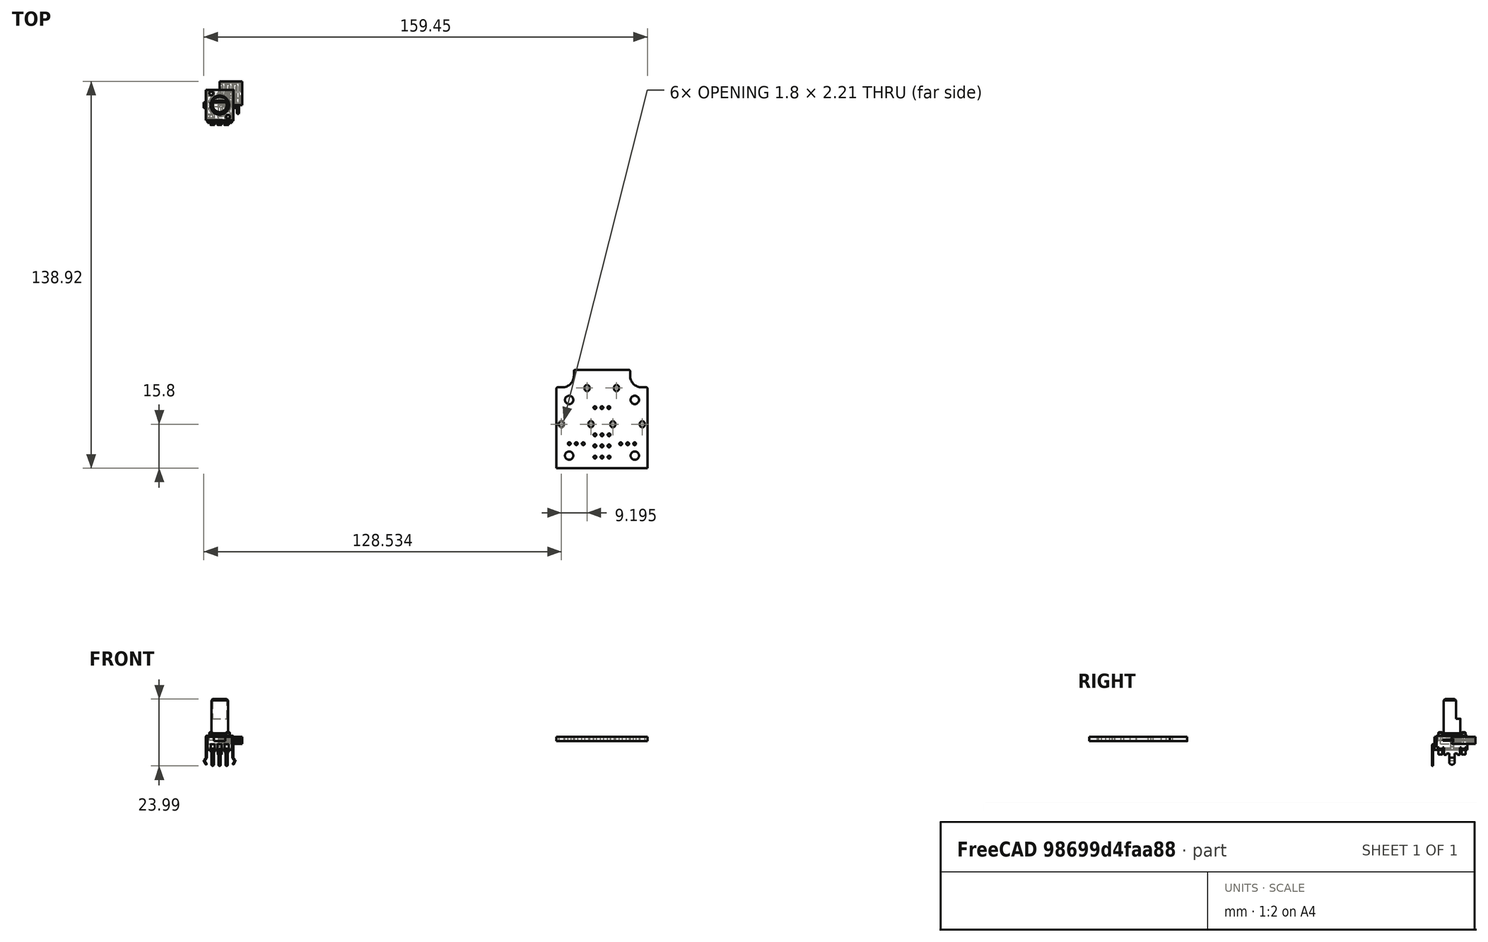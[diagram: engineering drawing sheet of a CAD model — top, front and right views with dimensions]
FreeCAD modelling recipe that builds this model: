
FCSTD DOCUMENT  (FreeCAD 0.20R25645 (Git))
Label: PotBoard
License: All rights reserved
LicenseURL: http://en.wikipedia.org/wiki/All_rights_reserved
objects: Part::Feature×7, App::Part×7, App::Link×4, PartDesign::CoordinateSystem×1, Sketcher::SketchObject×1
note: 9 computed .brp shape members not serialized (recipe doc carries the construction recipe); baked Part::Feature solids carry a one-line shape summary decoded from their .brp

FEATURE [PartDesign::CoordinateSystem] Local_CS_873f
  AttacherType = Attacher::AttachEngine3D
FEATURE [Part::Feature] Pcb_873f
  shape: bbox 32.7 x 35.3 x 1.6 mm, 86 faces (baked)
FEATURE [Sketcher::SketchObject] PCB_Sketch_873f
  FullyConstrained = false
  sketch-geometry (126):
    g0: LineSegment StartX=121.055 StartY=-101.87 StartZ=0 EndX=121.055 EndY=-130.418 EndZ=0
    g1: LineSegment StartX=127.305 StartY=-95.6198 StartZ=0 EndX=127.305 EndY=-97.218 EndZ=0
    g2: LineSegment StartX=123.153 StartY=-101.37 StartZ=0 EndX=121.555 EndY=-101.37 EndZ=0
    g3: LineSegment StartX=153.251 StartY=-101.37 StartZ=0 EndX=151.653 EndY=-101.37 EndZ=0
    g4: LineSegment StartX=153.751 StartY=-130.418 StartZ=0 EndX=153.751 EndY=-101.87 EndZ=0
    g5: LineSegment StartX=147.001 StartY=-95.1202 StartZ=0 EndX=127.805 EndY=-95.1202 EndZ=0
    g6: LineSegment StartX=121.055 StartY=-130.418 StartZ=0 EndX=153.751 EndY=-130.418 EndZ=0
    g7: LineSegment StartX=147.501 StartY=-97.218 StartZ=0 EndX=147.501 EndY=-95.6198 EndZ=0
    g8: BSplineCurve PolesCount=4 KnotsCount=2 Degree=3 IsPeriodic=0
    g9: BSplineCurve PolesCount=4 KnotsCount=2 Degree=3 IsPeriodic=0
    g10: BSplineCurve PolesCount=4 KnotsCount=2 Degree=3 IsPeriodic=0
    g11: BSplineCurve PolesCount=4 KnotsCount=2 Degree=3 IsPeriodic=0
    g12: BSplineCurve PolesCount=4 KnotsCount=2 Degree=3 IsPeriodic=0
    g13: BSplineCurve PolesCount=4 KnotsCount=2 Degree=3 IsPeriodic=0
    g14: BSplineCurve PolesCount=4 KnotsCount=2 Degree=3 IsPeriodic=0
    g15: BSplineCurve PolesCount=4 KnotsCount=2 Degree=3 IsPeriodic=0
    g16: BSplineCurve PolesCount=4 KnotsCount=2 Degree=3 IsPeriodic=0
    g17: BSplineCurve PolesCount=4 KnotsCount=2 Degree=3 IsPeriodic=0
    g18: BSplineCurve PolesCount=4 KnotsCount=2 Degree=3 IsPeriodic=0
    g19: BSplineCurve PolesCount=4 KnotsCount=2 Degree=3 IsPeriodic=0
    g20: BSplineCurve PolesCount=4 KnotsCount=2 Degree=3 IsPeriodic=0
    g21: BSplineCurve PolesCount=4 KnotsCount=2 Degree=3 IsPeriodic=0
    g22: BSplineCurve PolesCount=4 KnotsCount=2 Degree=3 IsPeriodic=0
    g23: BSplineCurve PolesCount=4 KnotsCount=2 Degree=3 IsPeriodic=0
    g24: ArcOfCircle CenterX=123.153 CenterY=-97.218 CenterZ=0 NormalX=0 NormalY=0 NormalZ=1 AngleXU=0 Radius=4.1522 StartAngle=4.71239 EndAngle=6.28319
    g25: ArcOfCircle CenterX=151.653 CenterY=-97.218 CenterZ=0 NormalX=0 NormalY=0 NormalZ=1 AngleXU=0 Radius=4.1522 StartAngle=3.14159 EndAngle=4.71239
    g26: Circle CenterX=125.603 CenterY=-125.918 CenterZ=0 NormalX=0 NormalY=0 NormalZ=1 AngleXU=0 Radius=1.5
    g27: Circle CenterX=149.203 CenterY=-125.918 CenterZ=0 NormalX=0 NormalY=0 NormalZ=1 AngleXU=0 Radius=1.5
    g28: Circle CenterX=149.203 CenterY=-105.918 CenterZ=0 NormalX=0 NormalY=0 NormalZ=1 AngleXU=0 Radius=1.5
    g29: Circle CenterX=125.603 CenterY=-105.918 CenterZ=0 NormalX=0 NormalY=0 NormalZ=1 AngleXU=0 Radius=1.5
    g30-g33: Circle x4 (B-spline internal-alignment scaffolding for g8; pole/knot coordinates omitted)
    g34: GeomPoint X=153.751 Y=-101.87 Z=0
    g35: GeomPoint X=153.713 Y=-101.679 Z=0
    g36-g39: Circle x4 (B-spline internal-alignment scaffolding for g9; pole/knot coordinates omitted)
    g40: GeomPoint X=121.555 Y=-101.37 Z=0
    g41: GeomPoint X=121.364 Y=-101.408 Z=0
    g42-g45: Circle x4 (B-spline internal-alignment scaffolding for g10; pole/knot coordinates omitted)
    g46: GeomPoint X=153.442 Y=-101.408 Z=0
    g47: GeomPoint X=153.251 Y=-101.37 Z=0
    g48-g51: Circle x4 (B-spline internal-alignment scaffolding for g11; pole/knot coordinates omitted)
    g52: GeomPoint X=127.805 Y=-95.1202 Z=0
    g53: GeomPoint X=127.614 Y=-95.1582 Z=0
    g54-g57: Circle x4 (B-spline internal-alignment scaffolding for g12; pole/knot coordinates omitted)
    g58: GeomPoint X=147.354 Y=-95.2666 Z=0
    g59: GeomPoint X=147.192 Y=-95.1582 Z=0
    g60-g63: Circle x4 (B-spline internal-alignment scaffolding for g13; pole/knot coordinates omitted)
    g64: GeomPoint X=147.192 Y=-95.1582 Z=0
    g65: GeomPoint X=147.001 Y=-95.1202 Z=0
    g66-g69: Circle x4 (B-spline internal-alignment scaffolding for g14; pole/knot coordinates omitted)
    g70: GeomPoint X=147.463 Y=-95.4287 Z=0
    g71: GeomPoint X=147.354 Y=-95.2666 Z=0
    g72-g75: Circle x4 (B-spline internal-alignment scaffolding for g15; pole/knot coordinates omitted)
    g76: GeomPoint X=147.501 Y=-95.6198 Z=0
    g77: GeomPoint X=147.463 Y=-95.4287 Z=0
    g78-g81: Circle x4 (B-spline internal-alignment scaffolding for g16; pole/knot coordinates omitted)
    g82: GeomPoint X=121.364 Y=-101.408 Z=0
    g83: GeomPoint X=121.202 Y=-101.517 Z=0
    g84-g87: Circle x4 (B-spline internal-alignment scaffolding for g17; pole/knot coordinates omitted)
    g88: GeomPoint X=153.604 Y=-101.517 Z=0
    g89: GeomPoint X=153.442 Y=-101.408 Z=0
    g90-g93: Circle x4 (B-spline internal-alignment scaffolding for g18; pole/knot coordinates omitted)
    g94: GeomPoint X=153.713 Y=-101.679 Z=0
    g95: GeomPoint X=153.604 Y=-101.517 Z=0
    g96-g99: Circle x4 (B-spline internal-alignment scaffolding for g19; pole/knot coordinates omitted)
    g100: GeomPoint X=127.343 Y=-95.4287 Z=0
    g101: GeomPoint X=127.305 Y=-95.6198 Z=0
    g102-g105: Circle x4 (B-spline internal-alignment scaffolding for g20; pole/knot coordinates omitted)
    g106: GeomPoint X=127.614 Y=-95.1582 Z=0
    g107: GeomPoint X=127.452 Y=-95.2666 Z=0
    g108-g111: Circle x4 (B-spline internal-alignment scaffolding for g21; pole/knot coordinates omitted)
    g112: GeomPoint X=127.452 Y=-95.2666 Z=0
    g113: GeomPoint X=127.343 Y=-95.4287 Z=0
    g114-g117: Circle x4 (B-spline internal-alignment scaffolding for g22; pole/knot coordinates omitted)
    g118: GeomPoint X=121.093 Y=-101.679 Z=0
    g119: GeomPoint X=121.055 Y=-101.87 Z=0
    g120-g123: Circle x4 (B-spline internal-alignment scaffolding for g23; pole/knot coordinates omitted)
    g124: GeomPoint X=121.202 Y=-101.517 Z=0
    g125: GeomPoint X=121.093 Y=-101.679 Z=0
  constraints (42):
    c: Coincident(g0,g6)
    c: Coincident(g0,g22)
    c: Coincident(g22,g23)
    c: Coincident(g23,g16)
    c: Coincident(g16,g9)
    c: Coincident(g2,g9)
    c: Coincident(g24,g2)
    c: Coincident(g1,g24)
    c: Coincident(g19,g1)
    c: Coincident(g21,g19)
    c: Coincident(g21,g20)
    c: Coincident(g20,g11)
    c: Coincident(g5,g11)
    c: Coincident(g5,g13)
    c: Coincident(g13,g12)
    c: Coincident(g14,g12)
    c: Coincident(g15,g14)
    c: Coincident(g25,g7)
    c: Coincident(g15,g7)
    c: Coincident(g25,g3)
    c: Coincident(g10,g3)
    c: Coincident(g10,g17)
    c: Coincident(g18,g17)
    c: Coincident(g8,g18)
    c: Coincident(g6,g4)
    c: Coincident(g8,g4)
    c: InternalAlignment(g30-g35 -> g8) x6
    c: InternalAlignment(g36-g41 -> g9) x6
    c: InternalAlignment(g42-g47 -> g10) x6
    c: InternalAlignment(g48-g53 -> g11) x6
    c: InternalAlignment(g54-g59 -> g12) x6
    c: InternalAlignment(g60-g65 -> g13) x6
    c: InternalAlignment(g66-g71 -> g14) x6
    c: InternalAlignment(g72-g77 -> g15) x6
    c: InternalAlignment(g78-g83 -> g16) x6
    c: InternalAlignment(g84-g89 -> g17) x6
    c: InternalAlignment(g90-g95 -> g18) x6
    c: InternalAlignment(g96-g101 -> g19) x6
    c: InternalAlignment(g102-g107 -> g20) x6
    c: InternalAlignment(g108-g113 -> g21) x6
    c: InternalAlignment(g114-g119 -> g22) x6
    c: InternalAlignment(g120-g125 -> g23) x6
FEATURE [App::Part] Board_Geoms_873f
  Group = -> [Local_CS_873f,Pcb_873f,PCB_Sketch_873f]
  Origin = -> Origin
FEATURE [Part::Feature] Part__Feature  label="_ _ _C031LFBN-RC"
  shape: bbox 2.03 x 10.73 x 0.4 mm, 28 faces (baked)
FEATURE [Part::Feature] Part__Feature001  label="_ _ _C031LFBN-RC001"
  shape: bbox 8.12 x 8.5 x 2.54 mm, 73 faces (baked)
FEATURE [Part::Feature] Part__Feature002  label="_ _ _C031LFBN-RC002"
  shape: bbox 2.03 x 10.73 x 0.4 mm, 28 faces (baked)
FEATURE [Part::Feature] Part__Feature003  label="_ _ _C031LFBN-RC003"
  shape: bbox 2.03 x 10.73 x 0.4 mm, 28 faces (baked)
FEATURE [App::Part] C031LFBN_RC  label="J3_C031LFBN-RC_61255B4B"
  Group = -> [Part__Feature,Part__Feature001,Part__Feature002,Part__Feature003]
  Origin = -> Origin008
  Placement = pos=(133.35,-121.158,-1.6) rot=(-1,0,0;1.5708rad)
FEATURE [App::Link] J3_C031LFBN_RC_61255B4B_ln_  label="J2_C031LFBN-RC_61255B34"
  LinkPlacement = pos=(141.478,-119.71,-1.6) rot=(0,0.707107,-0.707107;3.14159rad)
  LinkedObject = -> C031LFBN_RC
  Placement = pos=(141.478,-119.71,-1.6) rot=(0,0.707107,-0.707107;3.14159rad)
FEATURE [App::Link] J3_C031LFBN_RC_61255B4B_ln_001  label="J1_C031LFBN-RC_6125D110"
  LinkPlacement = pos=(133.35,-125.171,-1.6) rot=(-1,0,0;1.5708rad)
  LinkedObject = -> C031LFBN_RC
  Placement = pos=(133.35,-125.171,-1.6) rot=(-1,0,0;1.5708rad)
FEATURE [App::Part] Bot_873f
  Group = -> [C031LFBN_RC,J3_C031LFBN_RC_61255B4B_ln_,J3_C031LFBN_RC_61255B4B_ln_001]
  Origin = -> Origin004
FEATURE [Part::Feature] Part__Feature004  label="PTV09A-4X20F-XXXCX"
  shape: bbox 6.1 x 6.1 x 17.1 mm, 13 faces (baked)
FEATURE [Part::Feature] Part__Feature005  label="PTV09A-4X20F-XXXCX001"
  shape: bbox 11.4 x 12.65 x 12.09 mm, 205 faces (baked)
FEATURE [App::Part] ptv09a_4x20f_xxxx  label="RV3_ptv09a-4x20f-xxxx_6149A4B8"
  Group = -> [Part__Feature004,Part__Feature005]
  Origin = -> Origin009
  Placement = pos=(146.632,-114.605,6.4516) rot=(0,0,1;0rad)
FEATURE [App::Link] RV3_ptv09a_4x20f_xxxx_6149A4B8_ln_  label="RV2_ptv09a-4x20f-xxxx_6149BC96"
  LinkPlacement = pos=(137.35,-101.603,6.4516) rot=(0,0,1;0rad)
  LinkedObject = -> ptv09a_4x20f_xxxx
  Placement = pos=(137.35,-101.603,6.4516) rot=(0,0,1;0rad)
FEATURE [App::Link] RV3_ptv09a_4x20f_xxxx_6149A4B8_ln_001  label="RV1_ptv09a-4x20f-xxxx_6149B2CC"
  LinkPlacement = pos=(128.156,-114.569,6.4516) rot=(0,0,1;0rad)
  LinkedObject = -> ptv09a_4x20f_xxxx
  Placement = pos=(128.156,-114.569,6.4516) rot=(0,0,1;0rad)
FEATURE [App::Part] Top_873f
  Group = -> [ptv09a_4x20f_xxxx,RV3_ptv09a_4x20f_xxxx_6149A4B8_ln_,RV3_ptv09a_4x20f_xxxx_6149A4B8_ln_001]
  Origin = -> Origin003
FEATURE [App::Part] Step_Models_873f
  Group = -> [Top_873f,Bot_873f]
  Origin = -> Origin002
FEATURE [App::Part] Board_873f  label="PotBoard"
  Group = -> [Board_Geoms_873f,Step_Models_873f]
  Origin = -> Origin001
